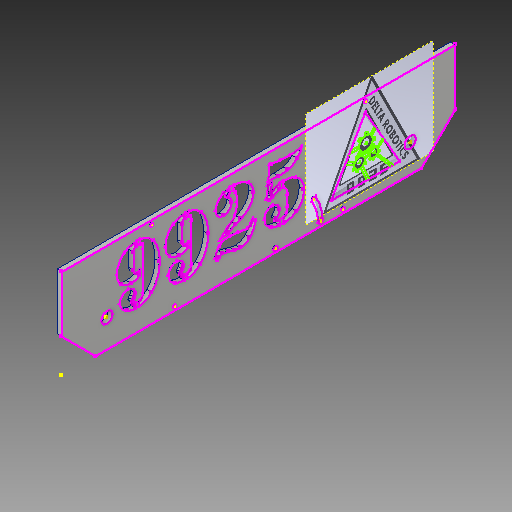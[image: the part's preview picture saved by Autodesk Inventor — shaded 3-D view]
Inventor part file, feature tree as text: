
AUTODESK INVENTOR PART (.ipt)
format: ipt  version: 2019 (Build 230136000, 136)  size: 1,378,816 bytes
history: native  units: in
note: dims shown in document units (in); Inventor stores cm internally (conversion verified against a paired STEP export)
features: sketch x6, extrude x4, projected_geometry x3, chamfer x2, hole x2, other x1
ambient origin geometry x8: Origin, YZ Plane, XZ Plane, XY Plane, X Axis, Y Axis, Z Axis, Center Point
bodies: Solid1 (feature_tree)
feature tree (18):
  extrude  "Extrusion1"  Depth=17.5in
  chamfer  "Chamfer1"  Distance=0.1875in
  chamfer  "Chamfer2"  Distance=1.5in Angle=45.0deg
  hole  "Hole3"  [1 undecoded]
  sketch  "Sketch9"  dims[d3=1.25in]
  hole  "Hole4"  [1 undecoded]
  extrude  "Extrusion6"  Depth=0.603in
  extrude  "Extrusion7"  Depth=0.125in
  extrude  "Extrusion8"  Depth=0.63in
  sketch  "Sketch13"  dims[d11=1.5in d12=0.125in d13=45.0deg d22=6.517in d23=0.125in d24=0.603in d25=0.125in d26=0.63in d27=6.517in d28=0.125in d29=0.603in d30=6.517in d31=0.125in d32=0.63in d33=6.517in d110=0.175in d111=0.175in d112=4.0in d113=4.0in d114=0.175in d115=0.175in d116=0.15in d117=0.75in d118=0.375in d119=0.25in d120=0.5635in d121=1.0in d122=0.8108in d123=5.0in d124=5.0in d125=8.0in d126=0.15in d127=0.2in d128=0.75in d129=0.375in d130=0.25in d131=0.5635in d132=1.0in d133=0.8108in d134=2.0in d135=0.2in d137=1.0in d138=0.0in d139=0.2in d140=1.0in d141=1.0in d142=0.0in d143=0.75in d144=0.75in d145=0.6033in d146=4.0in d147=0.0in d148=0.0in]
  sketch  "Sketch1"  dims[d0=4.0in d1=17.5in]
  sketch  "Sketch8"  dims[d2=0.501in]
  projected_geometry  "Projected Loop7"
  sketch  "Sketch10"  dims[d4=2.0in]
  sketch  "Sketch11"  dims[d5=2.0in d6=0.1875in d7=0.0in d8=1.5in d9=0.125in d10=45.0deg]
  other  "Image1"
  projected_geometry  "Projected Loop8"
  projected_geometry  "Projected Loop9"
note: 2 required parameter values undecoded (feature->parameter linkage not recoverable at this tier; creation-order binding heuristic only, values carry confidence <= 0.55)
